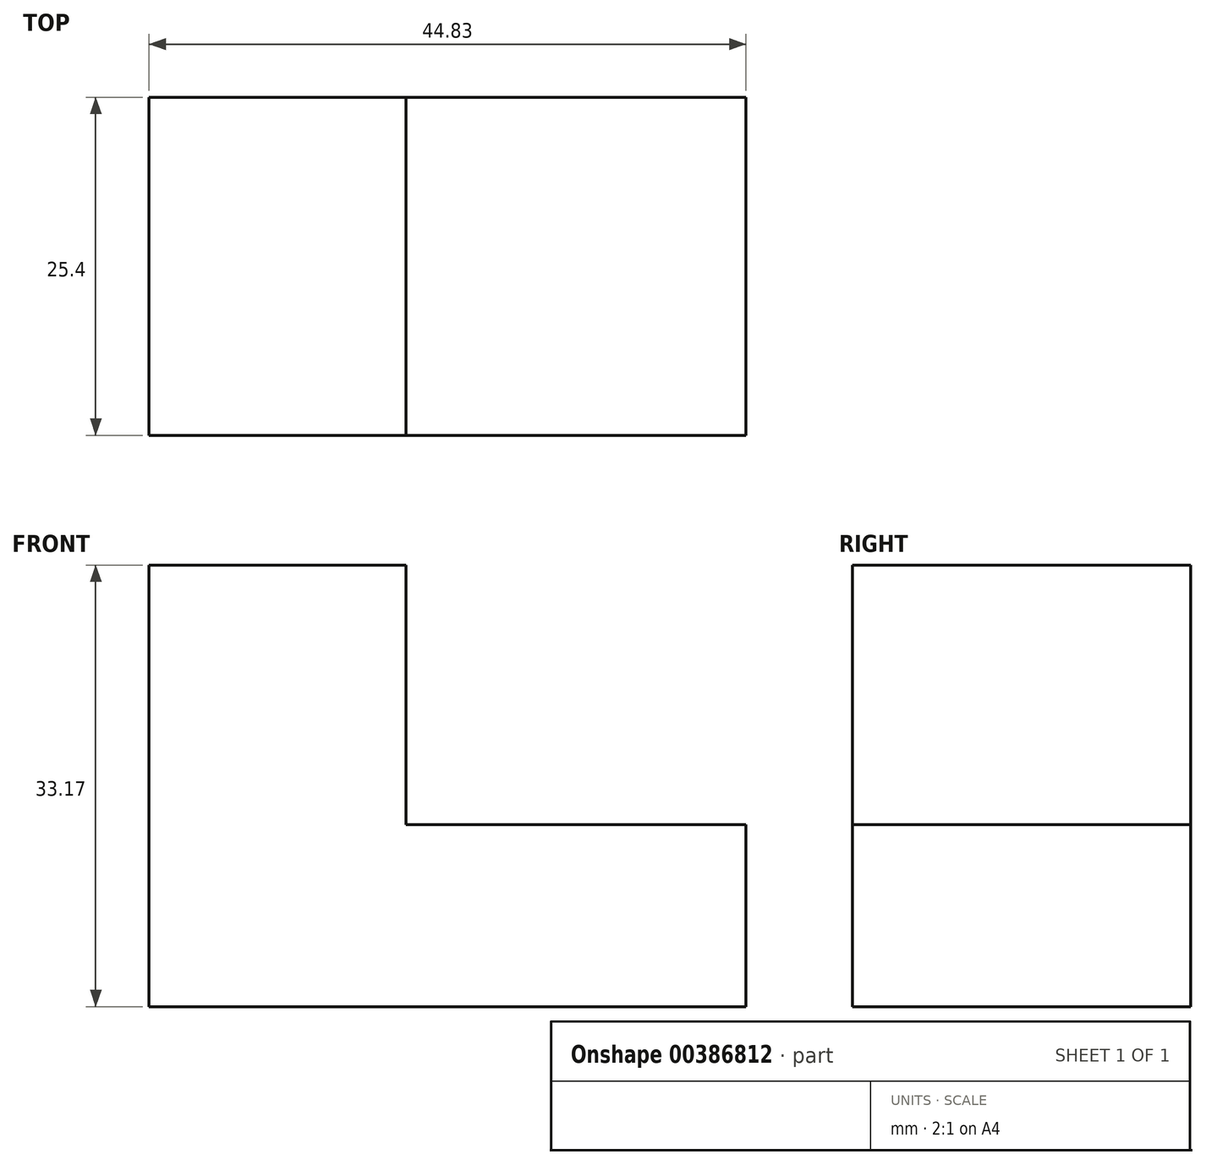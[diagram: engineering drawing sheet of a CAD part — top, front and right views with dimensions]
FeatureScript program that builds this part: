
annotation { "Feature Type Name" : "Feature", "Feature Type Description" : "" }
export const myFeature = defineFeature(function(context is Context, id is Id, definition is map)
    precondition{}
    {
        {
            var Q0;
            Q0=qCreatedBy(makeId("Front.planeOp"),FACE);
            var sketch = newSketch(context, id + "F0", { "sketchPlane" : qUnion([Q0])});
            skLineSegment(sketch, "E0", {"start": v(0, 0) * mm, "end": v(0, 33.17) * mm});
            skLineSegment(sketch, "E1", {"start": v(0, 33.17) * mm, "end": v(19.3, 33.17) * mm});
            skLineSegment(sketch, "E2", {"start": v(19.3, 33.17) * mm, "end": v(19.3, 13.67) * mm});
            skLineSegment(sketch, "E3", {"start": v(19.3, 13.67) * mm, "end": v(44.83, 13.67) * mm});
            skLineSegment(sketch, "E4", {"start": v(44.83, 13.67) * mm, "end": v(44.83, 0) * mm});
            skLineSegment(sketch, "E5", {"start": v(44.83, 0) * mm, "end": v(0, 0) * mm});
            skSolve(sketch);
        }
        {
            var Q0;
            Q0=makeQuery(id+"F0.imprint","IMPRINT",FACE,{"disambiguationData":[TD([[makeQuery(id+"F0.imprint","IMPRINT",EDGE,{"derivedFrom":sQuery(id+"F0.wireOp",EDGE,"E0")}),-1.0]])]});
            extrude(context, id + "F1", {"entities" : qUnion([Q0]), "depth" : 25.4 * mm});
        }
    });
